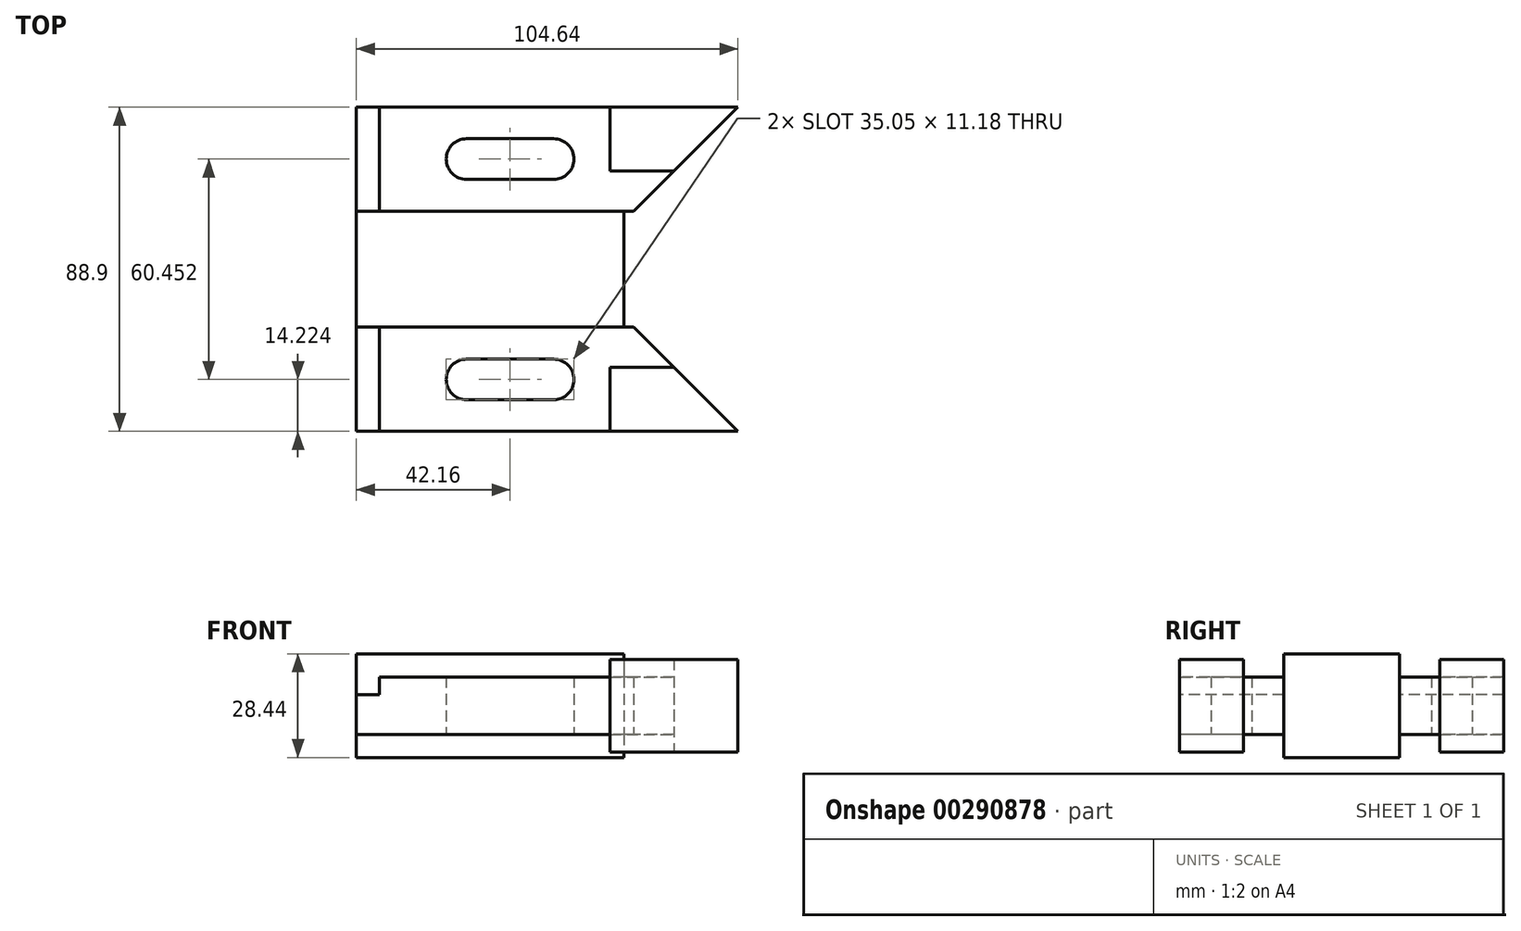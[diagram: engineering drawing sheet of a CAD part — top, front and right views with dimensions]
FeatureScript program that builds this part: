
annotation { "Feature Type Name" : "Feature", "Feature Type Description" : "" }
export const myFeature = defineFeature(function(context is Context, id is Id, definition is map)
    precondition{}
    {
        {
            var Q0;
            Q0=qCreatedBy(makeId("Top.planeOp"),FACE);
            var sketch = newSketch(context, id + "F0", { "sketchPlane" : qUnion([Q0])});
            skLineSegment(sketch, "E0.bottom", {"start": v(52.32, 44.45) * mm, "end": v(-52.32, 44.45) * mm});
            skLineSegment(sketch, "E0.top", {"start": v(52.32, -44.45) * mm, "end": v(-52.32, -44.45) * mm});
            skLineSegment(sketch, "E0.right", {"start": v(-52.32, 44.45) * mm, "end": v(-52.32, -44.45) * mm});
            skPoint(sketch, "E0.middle", {"position": v(0, 0) * mm});
            skLineSegment(sketch, "E1.bottom", {"start": v(21.08, 15.88) * mm, "end": v(-52.32, 15.88) * mm});
            skLineSegment(sketch, "E1.top", {"start": v(21.08, -15.88) * mm, "end": v(-52.32, -15.88) * mm});
            skLineSegment(sketch, "E1.left", {"start": v(21.08, 15.88) * mm, "end": v(21.08, -15.87) * mm});
            skPoint(sketch, "E1.middle", {"position": v(-52.32, 0) * mm});
            skPoint(sketch, "E1.right.end.orphan", {"position": v(-125.73, -15.87) * mm});
            skPoint(sketch, "E1.right.start.orphan", {"position": v(-125.73, 15.88) * mm});
            skLineSegment(sketch, "E2", {"start": v(52.32, -44.45) * mm, "end": v(23.75, -15.87) * mm});
            skLineSegment(sketch, "E3", {"start": v(-67.59, 0) * mm, "end": v(76.25, 0) * mm, "construction": true});
            skLineSegment(sketch, "E4.MirrorCS", {"start": v(52.32, 44.45) * mm, "end": v(23.75, 15.88) * mm});
            skLineSegment(sketch, "E5", {"start": v(23.75, 15.88) * mm, "end": v(21.08, 15.88) * mm});
            skLineSegment(sketch, "E6", {"start": v(23.75, -15.87) * mm, "end": v(21.08, -15.88) * mm});
            skLineSegment(sketch, "E7", {"start": v(17.27, -26.92) * mm, "end": v(34.8, -26.92) * mm});
            skLineSegment(sketch, "E8", {"start": v(17.27, -26.92) * mm, "end": v(17.27, -44.45) * mm});
            skLineSegment(sketch, "E9.MirrorCS", {"start": v(17.27, 26.92) * mm, "end": v(34.8, 26.92) * mm});
            skLineSegment(sketch, "E10.MirrorCS", {"start": v(17.27, 26.92) * mm, "end": v(17.27, 44.45) * mm});
            skLineSegment(sketch, "E11", {"start": v(-45.97, 44.45) * mm, "end": v(-45.97, 15.88) * mm});
            skLineSegment(sketch, "E12.MirrorCS", {"start": v(-45.97, -44.45) * mm, "end": v(-45.97, -15.87) * mm});
            skLineSegment(sketch, "E13", {"start": v(-52.32, -30.23) * mm, "end": v(-27.69, -30.23) * mm, "construction": true});
            skLineSegment(sketch, "E14", {"start": v(-22.1, -24.64) * mm, "end": v(1.78, -24.64) * mm});
            skLineSegment(sketch, "E15", {"start": v(1.78, -35.81) * mm, "end": v(-22.1, -35.81) * mm});
            skArc(sketch, "E16", {"start": v(-22.1, -24.64) * mm, "mid": v(-27.69, -30.23) * mm, "end": v(-22.1, -35.81) * mm});
            skLineSegment(sketch, "E17", {"start": v(-10.16, -24.64) * mm, "end": v(-10.16, -35.81) * mm, "construction": true});
            skArc(sketch, "E18.MirrorC", {"start": v(1.78, -24.64) * mm, "mid": v(7.37, -30.23) * mm, "end": v(1.78, -35.81) * mm});
            skPoint(sketch, "E19.end.orphan", {"position": v(-27.69, -24.64) * mm});
            skPoint(sketch, "E20.orphan", {"position": v(-27.69, -35.81) * mm});
            skPoint(sketch, "E21.orphan", {"position": v(7.37, -24.64) * mm});
            skPoint(sketch, "E22.orphan", {"position": v(7.37, -35.81) * mm});
            skLineSegment(sketch, "E23.MirrorCS", {"start": v(-22.1, 24.64) * mm, "end": v(1.78, 24.64) * mm});
            skArc(sketch, "E24.MirrorCS", {"start": v(1.78, 24.64) * mm, "mid": v(7.37, 30.23) * mm, "end": v(1.78, 35.81) * mm});
            skLineSegment(sketch, "E25.MirrorCS", {"start": v(1.78, 35.81) * mm, "end": v(-22.1, 35.81) * mm});
            skArc(sketch, "E26.MirrorCS", {"start": v(-22.1, 24.64) * mm, "mid": v(-27.69, 30.23) * mm, "end": v(-22.1, 35.81) * mm});
            skSolve(sketch);
        }
        {
            var Q0;
            {var subQ0=sQuery(id+"F0.wireOp",EDGE,"E1.left");Q0=makeQuery(id+"F0.imprint","IMPRINT",FACE,{"disambiguationData":[TD([[makeQuery(id+"F0.imprint","IMPRINT",EDGE,{"derivedFrom":subQ0}),-1.0]])]});}
            extrude(context, id + "F1", {"entities" : qUnion([Q0]), "endBound" : BoundingType.SYMMETRIC, "depth" : 28.45 * mm});
        }
        {
            var Q0;
            {var subQ4=sQuery(id+"F0.wireOp",EDGE,"E9.MirrorCS");Q0=makeQuery(id+"F0.imprint","IMPRINT",FACE,{"disambiguationData":[TD([[makeQuery(id+"F0.imprint","IMPRINT",EDGE,{"derivedFrom":subQ4}),1.0]])]});}
            var Q1;
            {var subQ4=sQuery(id+"F0.wireOp",EDGE,"E7");Q1=makeQuery(id+"F0.imprint","IMPRINT",FACE,{"disambiguationData":[TD([[makeQuery(id+"F0.imprint","IMPRINT",EDGE,{"derivedFrom":subQ4}),-1.0]])]});}
            extrude(context, id + "F2", {"entities" : qUnion([Q0, Q1]), "endBound" : BoundingType.SYMMETRIC, "depth" : 25.4 * mm});
        }
        {
            var Q0;
            {var subQ0=sQuery(id+"F0.wireOp",EDGE,"E5");Q0=makeQuery(id+"F0.imprint","IMPRINT",FACE,{"disambiguationData":[TD([[makeQuery(id+"F0.imprint","IMPRINT",EDGE,{"derivedFrom":subQ0}),-1.0]])]});}
            var Q1;
            {var subQ4=sQuery(id+"F0.wireOp",EDGE,"E6");Q1=makeQuery(id+"F0.imprint","IMPRINT",FACE,{"disambiguationData":[TD([[makeQuery(id+"F0.imprint","IMPRINT",EDGE,{"derivedFrom":subQ4}),1.0]])]});}
            extrude(context, id + "F3", {"entities" : qUnion([Q0, Q1]), "endBound" : BoundingType.SYMMETRIC, "depth" : 15.75 * mm});
        }
        {
            var Q0;
            {var subQ3=sQuery(id+"F0.wireOp",EDGE,"E12.MirrorCS");Q0=makeQuery(id+"F0.imprint","IMPRINT",FACE,{"disambiguationData":[TD([[makeQuery(id+"F0.imprint","IMPRINT",EDGE,{"derivedFrom":subQ3}),1.0]])]});}
            var Q1;
            {var subQ3=sQuery(id+"F0.wireOp",EDGE,"E11");Q1=makeQuery(id+"F0.imprint","IMPRINT",FACE,{"disambiguationData":[TD([[makeQuery(id+"F0.imprint","IMPRINT",EDGE,{"derivedFrom":subQ3}),-1.0]])]});}
            extrude(context, id + "F4", {"entities" : qUnion([Q0, Q1]), "oppositeDirection" : true, "depth" : 7.87 * mm});
        }
        {
            var Q0;
            {var subQ3=sQuery(id+"F0.wireOp",EDGE,"E11");Q0=makeQuery(id+"F0.imprint","IMPRINT",FACE,{"disambiguationData":[TD([[makeQuery(id+"F0.imprint","IMPRINT",EDGE,{"derivedFrom":subQ3}),-1.0]])]});}
            var Q1;
            {var subQ3=sQuery(id+"F0.wireOp",EDGE,"E12.MirrorCS");Q1=makeQuery(id+"F0.imprint","IMPRINT",FACE,{"disambiguationData":[TD([[makeQuery(id+"F0.imprint","IMPRINT",EDGE,{"derivedFrom":subQ3}),1.0]])]});}
            extrude(context, id + "F5", {"entities" : qUnion([Q0, Q1]), "operationType" : NewBodyOperationType.ADD, "depth" : 3.05 * mm});
        }
    });
